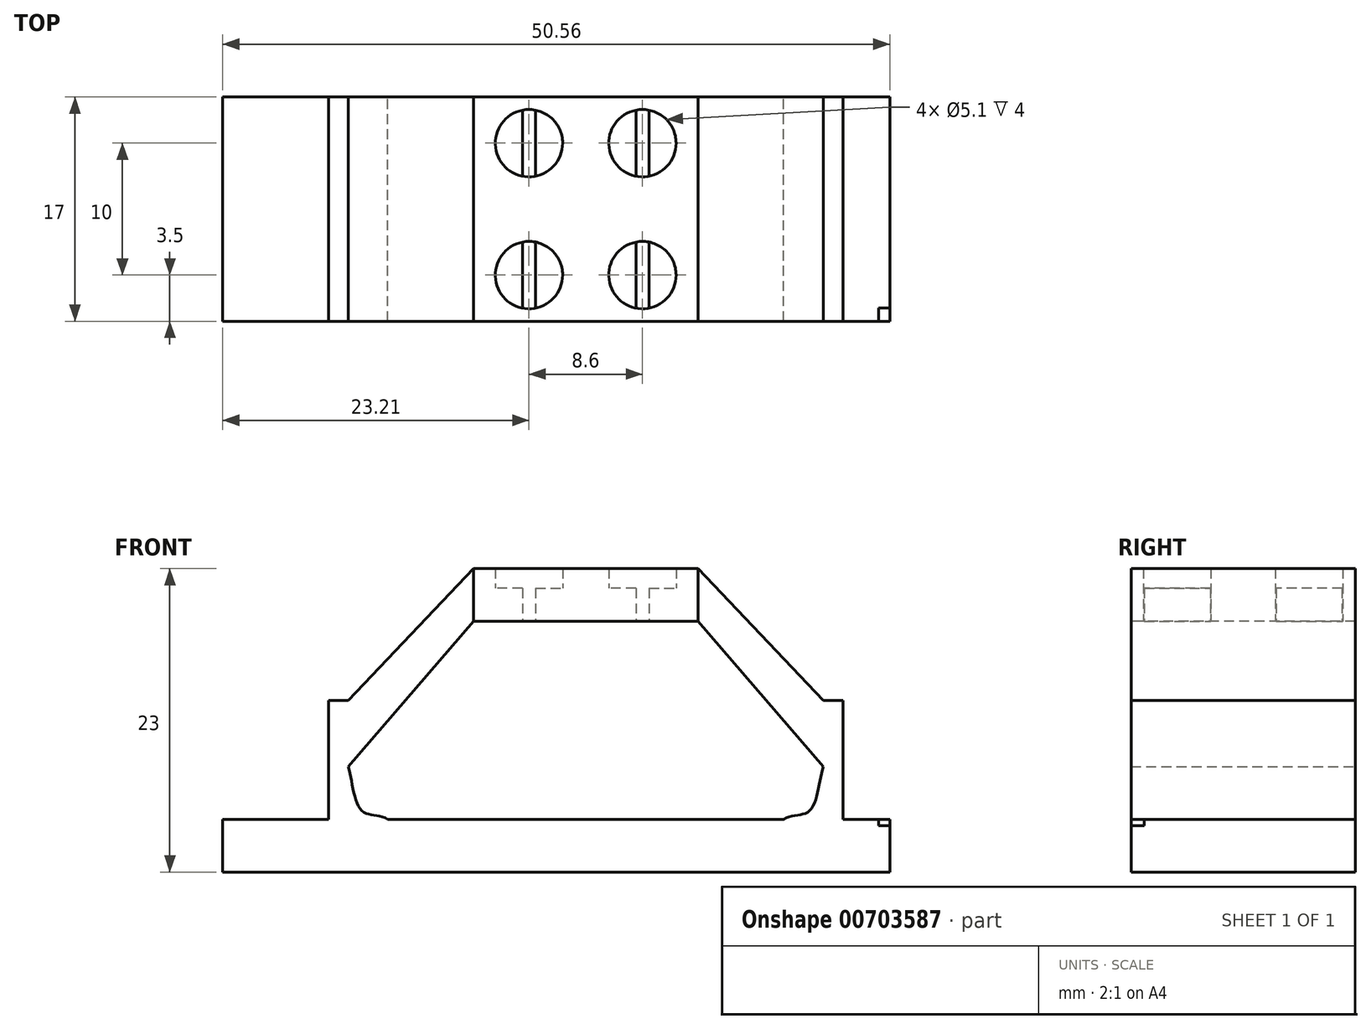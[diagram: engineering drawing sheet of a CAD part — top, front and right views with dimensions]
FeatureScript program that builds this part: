
annotation { "Feature Type Name" : "Feature", "Feature Type Description" : "" }
export const myFeature = defineFeature(function(context is Context, id is Id, definition is map)
    precondition{}
    {
        {
            assignVariable(context, id + "F0", {"name" : "Hollow", "anyValue" : 82});
        }
        {
            assignVariable(context, id + "F1", {"name" : "BaseThicknes", "anyValue" : 4});
        }
        {
            var Q0;
            Q0=qCreatedBy(makeId("Top.planeOp"),FACE);
            cPlane(context, id + "F2", {"entities" : qUnion([Q0]), "cplaneType" : CPlaneType.OFFSET, "offset" : (sqrt((sqrt((getVariable(context, 'Hollow') * getVariable(context, 'Hollow')) - ((getVariable(context, 'Hollow') / 2) * (getVariable(context, 'Hollow') / 2)))) * (sqrt((getVariable(context, 'Hollow') * getVariable(context, 'Hollow')) - ((getVariable(context, 'Hollow') / 2) * (getVariable(context, 'Hollow') / 2)))) - ((getVariable(context, 'Hollow') / 2) * (getVariable(context, 'Hollow') / 2)))) * mm, "width" : 150 * mm, "height" : 150 * mm});
        }
        {
            var Q0;
            Q0=qCreatedBy(id+"F2.planeOp",FACE);
            var sketch = newSketch(context, id + "F3", { "sketchPlane" : qUnion([Q0])});
            skPoint(sketch, "E0", {"position": v(0, 0) * mm});
            skSolve(sketch);
        }
        {
            var Q0;
            Q0=qCreatedBy(makeId("Top.planeOp"),FACE);
            var sketch = newSketch(context, id + "F4", { "sketchPlane" : qUnion([Q0])});
            skLineSegment(sketch, "E1.bottom", {"start": v(-41, 41) * mm, "end": v(41, 41) * mm});
            skLineSegment(sketch, "E1.top", {"start": v(-41, -41) * mm, "end": v(41, -41) * mm});
            skLineSegment(sketch, "E1.left", {"start": v(-41, 41) * mm, "end": v(-41, -41) * mm});
            skLineSegment(sketch, "E1.right", {"start": v(41, 41) * mm, "end": v(41, -41) * mm});
            skSolve(sketch);
        }
        {
            var Q0;
            Q0=qSketchRegion(id+"F4",true);
            extrude(context, id + "F5", {"entities" : qUnion([Q0]), "depth" : (getVariable(context, 'BaseThicknes')) * mm, "offsetDistance" : 25 * mm});
        }
        {
            var Q1;
            Q1=makeQuery(id+"F5.opExtrude","CAP_FACE",FACE,{"disambiguationData":[OSD([sQuery(id+"F4.wireOp",EDGE,"E1.bottom"),sQuery(id+"F4.wireOp",EDGE,"E1.top"),sQuery(id+"F4.wireOp",EDGE,"E1.left"),sQuery(id+"F4.wireOp",EDGE,"E1.right")])],"isStart":true});
            var Q2;
            Q2=sQuery(id+"F3.wireOp",VERTEX,"E0");
            loft(context, id + "F6", {"operationType" : NewBodyOperationType.INTERSECT, "sheetProfilesArray" : [{ "sheetProfileEntities" : qUnion([Q1]) }, { "sheetProfileEntities" : qUnion([Q2]) }]});
        }
        {
            var Q0;
            Q0=makeQuery(id+"F5.opExtrude","CAP_FACE",FACE,{"disambiguationData":[OSD([sQuery(id+"F4.wireOp",EDGE,"E1.bottom"),sQuery(id+"F4.wireOp",EDGE,"E1.top"),sQuery(id+"F4.wireOp",EDGE,"E1.left"),sQuery(id+"F4.wireOp",EDGE,"E1.right")])],"isStart":true});
            var sketch = newSketch(context, id + "F7", { "sketchPlane" : qUnion([Q0])});
            skCircle(sketch, "E2", {"center": v(-34.94, -34.94) * mm, "radius": 0.76 * mm});
            skCircle(sketch, "E3.MirrorC", {"center": v(34.94, -34.94) * mm, "radius": 0.76 * mm});
            skCircle(sketch, "E4.MirrorC", {"center": v(34.94, 34.94) * mm, "radius": 0.76 * mm});
            skCircle(sketch, "E5.MirrorC", {"center": v(-34.94, 34.94) * mm, "radius": 0.76 * mm});
            skCircle(sketch, "E6", {"center": v(-34.94, -34.94) * mm, "radius": 1.51 * mm});
            skCircle(sketch, "E7.MirrorC", {"center": v(-34.94, 34.94) * mm, "radius": 1.51 * mm});
            skCircle(sketch, "E8.MirrorC", {"center": v(34.94, -34.94) * mm, "radius": 1.51 * mm});
            skCircle(sketch, "E9.MirrorC", {"center": v(34.94, 34.94) * mm, "radius": 1.51 * mm});
            skSolve(sketch);
        }
        {
            var Q0;
            Q0=makeQuery(id+"F7.imprint","IMPRINT",FACE,{"disambiguationData":[TD([[makeQuery(id+"F7.imprint","IMPRINT",EDGE,{"derivedFrom":sQuery(id+"F7.wireOp",EDGE,"E2")}),1.0]])]});
            var Q1;
            Q1=makeQuery(id+"F7.imprint","IMPRINT",FACE,{"disambiguationData":[TD([[makeQuery(id+"F7.imprint","IMPRINT",EDGE,{"derivedFrom":sQuery(id+"F7.wireOp",EDGE,"E5.MirrorC")}),-1.0]])]});
            var Q2;
            Q2=makeQuery(id+"F7.imprint","IMPRINT",FACE,{"disambiguationData":[TD([[makeQuery(id+"F7.imprint","IMPRINT",EDGE,{"derivedFrom":sQuery(id+"F7.wireOp",EDGE,"E4.MirrorC")}),1.0]])]});
            var Q3;
            Q3=makeQuery(id+"F7.imprint","IMPRINT",FACE,{"disambiguationData":[TD([[makeQuery(id+"F7.imprint","IMPRINT",EDGE,{"derivedFrom":sQuery(id+"F7.wireOp",EDGE,"E3.MirrorC")}),-1.0]])]});
            extrude(context, id + "F8", {"entities" : qUnion([Q0, Q1, Q2, Q3]), "operationType" : NewBodyOperationType.REMOVE, "oppositeDirection" : true, "depth" : 25 * mm, "offsetDistance" : 25 * mm});
        }
        {
            var Q0;
            Q0=makeQuery(id+"F7.imprint","IMPRINT",FACE,{"disambiguationData":[TD([[makeQuery(id+"F7.imprint","IMPRINT",EDGE,{"derivedFrom":sQuery(id+"F7.wireOp",EDGE,"E5.MirrorC")}),1.0]])]});
            var Q1;
            Q1=makeQuery(id+"F7.imprint","IMPRINT",FACE,{"disambiguationData":[TD([[makeQuery(id+"F7.imprint","IMPRINT",EDGE,{"derivedFrom":sQuery(id+"F7.wireOp",EDGE,"E4.MirrorC")}),-1.0]])]});
            var Q2;
            Q2=makeQuery(id+"F7.imprint","IMPRINT",FACE,{"disambiguationData":[TD([[makeQuery(id+"F7.imprint","IMPRINT",EDGE,{"derivedFrom":sQuery(id+"F7.wireOp",EDGE,"E2")}),-1.0]])]});
            var Q3;
            Q3=makeQuery(id+"F7.imprint","IMPRINT",FACE,{"disambiguationData":[TD([[makeQuery(id+"F7.imprint","IMPRINT",EDGE,{"derivedFrom":sQuery(id+"F7.wireOp",EDGE,"E3.MirrorC")}),1.0]])]});
            extrude(context, id + "F9", {"entities" : qUnion([Q0, Q1, Q2, Q3]), "operationType" : NewBodyOperationType.REMOVE, "oppositeDirection" : true, "depth" : 2 * mm, "offsetDistance" : 25 * mm});
        }
        {
            var Q0;
            Q0=makeQuery(id+"F5.opExtrude","CAP_FACE",FACE,{"disambiguationData":[OSD([sQuery(id+"F4.wireOp",EDGE,"E1.bottom"),sQuery(id+"F4.wireOp",EDGE,"E1.top"),sQuery(id+"F4.wireOp",EDGE,"E1.left"),sQuery(id+"F4.wireOp",EDGE,"E1.right")])],"isStart":false});
            var sketch = newSketch(context, id + "F10", { "sketchPlane" : qUnion([Q0])});
            skLineSegment(sketch, "E10.bottom", {"start": v(-30, 29.5) * mm, "end": v(-26.3, 29.5) * mm});
            skLineSegment(sketch, "E10.top", {"start": v(-30, -16.5) * mm, "end": v(-26.3, -16.5) * mm});
            skLineSegment(sketch, "E10.left", {"start": v(-30, 29.5) * mm, "end": v(-30, -16.5) * mm});
            skLineSegment(sketch, "E10.right", {"start": v(-19.5, 29.5) * mm, "end": v(-19.5, -16.5) * mm});
            skLineSegment(sketch, "E11.bottom", {"start": v(-31.5, 31.5) * mm, "end": v(-26.3, 31.5) * mm});
            skLineSegment(sketch, "E11.top", {"start": v(-31.5, -18.5) * mm, "end": v(-18, -18.5) * mm});
            skLineSegment(sketch, "E11.left", {"start": v(-31.5, 31.5) * mm, "end": v(-31.5, -18.5) * mm});
            skLineSegment(sketch, "E11.right", {"start": v(-18, 31.5) * mm, "end": v(-18, -18.5) * mm});
            skLineSegment(sketch, "E12", {"start": v(-30, 27.7) * mm, "end": v(-28, 27.7) * mm});
            skLineSegment(sketch, "E13", {"start": v(-30, 28.7) * mm, "end": v(-28, 28.7) * mm});
            skLineSegment(sketch, "E14.left", {"start": v(-21.5, 28.7) * mm, "end": v(-21.5, 27.7) * mm});
            skLineSegment(sketch, "E14.right", {"start": v(-28, 28.7) * mm, "end": v(-28, 27.7) * mm});
            skLineSegment(sketch, "E15", {"start": v(-18, 6.5) * mm, "end": v(-31.5, 6.5) * mm, "construction": true});
            skLineSegment(sketch, "E16.trimOffspring", {"start": v(-21.5, 27.7) * mm, "end": v(-19.5, 27.7) * mm});
            skLineSegment(sketch, "E17.trimOffspring", {"start": v(-21.5, 28.7) * mm, "end": v(-19.5, 28.7) * mm});
            skLineSegment(sketch, "E18.MirrorCS", {"start": v(-30, -15.7) * mm, "end": v(-28, -15.7) * mm});
            skLineSegment(sketch, "E19.MirrorCS", {"start": v(-30, -14.7) * mm, "end": v(-28, -14.7) * mm});
            skLineSegment(sketch, "E20.MirrorCS", {"start": v(-21.5, -15.7) * mm, "end": v(-21.5, -14.7) * mm});
            skLineSegment(sketch, "E21.MirrorCS", {"start": v(-21.5, -15.7) * mm, "end": v(-19.5, -15.7) * mm});
            skLineSegment(sketch, "E22.MirrorCS", {"start": v(-21.5, -14.7) * mm, "end": v(-19.5, -14.7) * mm});
            skLineSegment(sketch, "E23.MirrorCS", {"start": v(-28, -15.7) * mm, "end": v(-28, -14.7) * mm});
            skLineSegment(sketch, "E24", {"start": v(-26.3, 31.5) * mm, "end": v(-26.3, 29.5) * mm});
            skLineSegment(sketch, "E25", {"start": v(-23.2, 31.5) * mm, "end": v(-23.2, 29.5) * mm});
            skLineSegment(sketch, "E26.trimOffspring", {"start": v(-23.2, 31.5) * mm, "end": v(-18, 31.5) * mm});
            skLineSegment(sketch, "E27.trimOffspring", {"start": v(-23.2, 29.5) * mm, "end": v(-19.5, 29.5) * mm});
            skLineSegment(sketch, "E28.MirrorCS", {"start": v(-26.3, -18.5) * mm, "end": v(-26.3, -16.5) * mm});
            skLineSegment(sketch, "E29.MirrorCS", {"start": v(-23.2, -18.5) * mm, "end": v(-23.2, -16.5) * mm});
            skLineSegment(sketch, "E30.trimOffspring", {"start": v(-23.2, -16.5) * mm, "end": v(-19.5, -16.5) * mm});
            skLineSegment(sketch, "E31.MirrorCS", {"start": v(21.5, 28.7) * mm, "end": v(21.5, 27.7) * mm});
            skLineSegment(sketch, "E32.MirrorCS", {"start": v(21.5, 28.7) * mm, "end": v(19.5, 28.7) * mm});
            skLineSegment(sketch, "E33.MirrorCS", {"start": v(23.2, 29.5) * mm, "end": v(19.5, 29.5) * mm});
            skLineSegment(sketch, "E34.MirrorCS", {"start": v(23.2, 31.5) * mm, "end": v(23.2, 29.5) * mm});
            skLineSegment(sketch, "E35.MirrorCS", {"start": v(28, -15.7) * mm, "end": v(28, -14.7) * mm});
            skLineSegment(sketch, "E36.MirrorCS", {"start": v(21.5, -15.7) * mm, "end": v(19.5, -15.7) * mm});
            skLineSegment(sketch, "E37.MirrorCS", {"start": v(23.2, -16.5) * mm, "end": v(19.5, -16.5) * mm});
            skLineSegment(sketch, "E38.MirrorCS", {"start": v(30, -15.7) * mm, "end": v(28, -15.7) * mm});
            skLineSegment(sketch, "E39.MirrorCS", {"start": v(21.5, -14.7) * mm, "end": v(19.5, -14.7) * mm});
            skLineSegment(sketch, "E40.MirrorCS", {"start": v(30, 29.5) * mm, "end": v(26.3, 29.5) * mm});
            skLineSegment(sketch, "E41.MirrorCS", {"start": v(30, 28.7) * mm, "end": v(28, 28.7) * mm});
            skLineSegment(sketch, "E42.MirrorCS", {"start": v(30, -16.5) * mm, "end": v(26.3, -16.5) * mm});
            skLineSegment(sketch, "E43.MirrorCS", {"start": v(26.3, 31.5) * mm, "end": v(26.3, 29.5) * mm});
            skLineSegment(sketch, "E44.MirrorCS", {"start": v(21.5, -15.7) * mm, "end": v(21.5, -14.7) * mm});
            skLineSegment(sketch, "E45.MirrorCS", {"start": v(28, 28.7) * mm, "end": v(28, 27.7) * mm});
            skLineSegment(sketch, "E46.MirrorCS", {"start": v(30, -14.7) * mm, "end": v(28, -14.7) * mm});
            skLineSegment(sketch, "E47.MirrorCS", {"start": v(31.5, 31.5) * mm, "end": v(26.3, 31.5) * mm});
            skLineSegment(sketch, "E48.MirrorCS", {"start": v(21.5, 27.7) * mm, "end": v(19.5, 27.7) * mm});
            skLineSegment(sketch, "E49.MirrorCS", {"start": v(23.2, -18.5) * mm, "end": v(23.2, -16.5) * mm});
            skLineSegment(sketch, "E50.MirrorCS", {"start": v(30, 27.7) * mm, "end": v(28, 27.7) * mm});
            skLineSegment(sketch, "E51.MirrorCS", {"start": v(26.3, -18.5) * mm, "end": v(26.3, -16.5) * mm});
            skLineSegment(sketch, "E52.MirrorCS", {"start": v(23.2, 31.5) * mm, "end": v(18, 31.5) * mm});
            skLineSegment(sketch, "E53.MirrorCS", {"start": v(31.5, 31.5) * mm, "end": v(31.5, -18.5) * mm});
            skLineSegment(sketch, "E54.MirrorCS", {"start": v(30, 29.5) * mm, "end": v(30, -16.5) * mm});
            skLineSegment(sketch, "E55.MirrorCS", {"start": v(31.5, -18.5) * mm, "end": v(18, -18.5) * mm});
            skLineSegment(sketch, "E56.MirrorCS", {"start": v(19.5, 29.5) * mm, "end": v(19.5, -16.5) * mm});
            skLineSegment(sketch, "E57.MirrorCS", {"start": v(18, 31.5) * mm, "end": v(18, -18.5) * mm});
            skLineSegment(sketch, "E58.MirrorCS", {"start": v(18, 6.5) * mm, "end": v(31.5, 6.5) * mm, "construction": true});
            skSolve(sketch);
        }
        {
            var Q0;
            {var subQ5=sQuery(id+"F10.wireOp",EDGE,"E33.MirrorCS");Q0=makeQuery(id+"F10.imprint","IMPRINT",FACE,{"disambiguationData":[TD([[makeQuery(id+"F10.imprint","IMPRINT",EDGE,{"derivedFrom":subQ5}),-1.0]])]});}
            var Q1;
            {var subQ6=sQuery(id+"F10.wireOp",EDGE,"E40.MirrorCS");Q1=makeQuery(id+"F10.imprint","IMPRINT",FACE,{"disambiguationData":[TD([[makeQuery(id+"F10.imprint","IMPRINT",EDGE,{"derivedFrom":subQ6}),-1.0]])]});}
            var Q2;
            Q2=makeQuery(id+"F10.imprint","IMPRINT",FACE,{"disambiguationData":[TD([[makeQuery(id+"F10.imprint","IMPRINT",EDGE,{"derivedFrom":sQuery(id+"F10.wireOp",EDGE,"E31.MirrorCS")}),-1.0]])]});
            var Q3;
            {var subQ0=sQuery(id+"F10.wireOp",EDGE,"E41.MirrorCS");Q3=makeQuery(id+"F10.imprint","IMPRINT",FACE,{"disambiguationData":[TD([[makeQuery(id+"F10.imprint","IMPRINT",EDGE,{"derivedFrom":subQ0}),1.0]])]});}
            var Q4;
            {var subQ0=sQuery(id+"F10.wireOp",EDGE,"E36.MirrorCS");Q4=makeQuery(id+"F10.imprint","IMPRINT",FACE,{"disambiguationData":[TD([[makeQuery(id+"F10.imprint","IMPRINT",EDGE,{"derivedFrom":subQ0}),-1.0]])]});}
            var Q5;
            Q5=makeQuery(id+"F10.imprint","IMPRINT",FACE,{"disambiguationData":[TD([[makeQuery(id+"F10.imprint","IMPRINT",EDGE,{"derivedFrom":sQuery(id+"F10.wireOp",EDGE,"E35.MirrorCS")}),-1.0]])]});
            var Q6;
            Q6=makeQuery(id+"F10.imprint","IMPRINT",FACE,{"disambiguationData":[TD([[makeQuery(id+"F10.imprint","IMPRINT",EDGE,{"derivedFrom":sQuery(id+"F10.wireOp",EDGE,"E20.MirrorCS")}),-1.0]])]});
            var Q7;
            {var subQ0=sQuery(id+"F10.wireOp",EDGE,"E18.MirrorCS");Q7=makeQuery(id+"F10.imprint","IMPRINT",FACE,{"disambiguationData":[TD([[makeQuery(id+"F10.imprint","IMPRINT",EDGE,{"derivedFrom":subQ0}),1.0]])]});}
            var Q8;
            {var subQ6=sQuery(id+"F10.wireOp",EDGE,"E10.bottom");Q8=makeQuery(id+"F10.imprint","IMPRINT",FACE,{"disambiguationData":[TD([[makeQuery(id+"F10.imprint","IMPRINT",EDGE,{"derivedFrom":subQ6}),1.0]])]});}
            var Q9;
            {var subQ0=sQuery(id+"F10.wireOp",EDGE,"E11.right");Q9=makeQuery(id+"F10.imprint","IMPRINT",FACE,{"disambiguationData":[TD([[makeQuery(id+"F10.imprint","IMPRINT",EDGE,{"derivedFrom":subQ0}),-1.0]])]});}
            var Q10;
            {var subQ0=sQuery(id+"F10.wireOp",EDGE,"E12");Q10=makeQuery(id+"F10.imprint","IMPRINT",FACE,{"disambiguationData":[TD([[makeQuery(id+"F10.imprint","IMPRINT",EDGE,{"derivedFrom":subQ0}),1.0]])]});}
            var Q11;
            Q11=makeQuery(id+"F10.imprint","IMPRINT",FACE,{"disambiguationData":[TD([[makeQuery(id+"F10.imprint","IMPRINT",EDGE,{"derivedFrom":sQuery(id+"F10.wireOp",EDGE,"E14.left")}),1.0]])]});
            extrude(context, id + "F11", {"entities" : qUnion([Q0, Q1, Q2, Q3, Q4, Q5, Q6, Q7, Q8, Q9, Q10, Q11]), "operationType" : NewBodyOperationType.ADD, "depth" : 9 * mm, "offsetDistance" : 25 * mm});
        }
        {
            var Q0;
            Q0=qCreatedBy(makeId("Front.planeOp"),FACE);
            var sketch = newSketch(context, id + "F12", { "sketchPlane" : qUnion([Q0])});
            skLineSegment(sketch, "E59", {"start": v(-31.5, 4) * mm, "end": v(-34.5, 4) * mm});
            skLineSegment(sketch, "E60", {"start": v(-31.5, 4) * mm, "end": v(-31.5, 8) * mm});
            skPoint(sketch, "E61", {"position": v(-34.5, 4) * mm});
            skFitSpline(sketch, "E62", {"points": [v(-31.5, 8) * mm, v(-32.53, 4.65) * mm, v(-34.5, 4) * mm], "startDerivative": vector(-1.67, -5.36) * mm, "endDerivative": vector(-4.69, -2.88) * mm});
            skLineSegment(sketch, "E63", {"start": v(-24.75, 13.95) * mm, "end": v(-24.75, 2.35) * mm, "construction": true});
            skFitSpline(sketch, "E64.MirrorCS", {"points": [v(-18, 8) * mm, v(-16.97, 4.65) * mm, v(-15, 4) * mm], "startDerivative": vector(1.67, -5.36) * mm, "endDerivative": vector(4.69, -2.88) * mm});
            skFitSpline(sketch, "E65.MirrorCS", {"points": [v(18, 8) * mm, v(16.97, 4.65) * mm, v(15, 4) * mm], "startDerivative": vector(-1.67, -5.36) * mm, "endDerivative": vector(-4.69, -2.88) * mm});
            skFitSpline(sketch, "E66.MirrorCS", {"points": [v(31.5, 8) * mm, v(32.53, 4.65) * mm, v(34.5, 4) * mm], "startDerivative": vector(1.67, -5.36) * mm, "endDerivative": vector(4.69, -2.88) * mm});
            skLineSegment(sketch, "E67.MirrorCS", {"start": v(-18, 4) * mm, "end": v(-15, 4) * mm});
            skLineSegment(sketch, "E68.MirrorCS", {"start": v(18, 4) * mm, "end": v(15, 4) * mm});
            skLineSegment(sketch, "E69.MirrorCS", {"start": v(31.5, 4) * mm, "end": v(34.5, 4) * mm});
            skLineSegment(sketch, "E70.MirrorCS", {"start": v(-18, 4) * mm, "end": v(-18, 8) * mm});
            skLineSegment(sketch, "E71.MirrorCS", {"start": v(18, 4) * mm, "end": v(18, 8) * mm});
            skLineSegment(sketch, "E72.MirrorCS", {"start": v(31.5, 4) * mm, "end": v(31.5, 8) * mm});
            skSolve(sketch);
        }
        {
            var Q0;
            Q0=qSketchRegion(id+"F12",true);
            extrude(context, id + "F13", {"entities" : qUnion([Q0]), "operationType" : NewBodyOperationType.ADD, "depth" : 18.5 * mm, "offsetDistance" : 25 * mm, "hasSecondDirection" : true, "secondDirectionOppositeDirection" : true, "secondDirectionDepth" : 31.5 * mm});
        }
        {
            var Q0;
            Q0=qCreatedBy(makeId("Right.planeOp"),FACE);
            var sketch = newSketch(context, id + "F14", { "sketchPlane" : qUnion([Q0])});
            skCircle(sketch, "E73", {"center": v(17.5, 13) * mm, "radius": 9 * mm});
            skCircle(sketch, "E74", {"center": v(-3.5, 13) * mm, "radius": 9 * mm});
            skSolve(sketch);
        }
        {
            var Q0;
            Q0=makeQuery(id+"F14.imprint","IMPRINT",FACE,{"disambiguationData":[TD([[makeQuery(id+"F14.imprint","IMPRINT",EDGE,{"derivedFrom":sQuery(id+"F14.wireOp",EDGE,"E73")}),1.0]])]});
            extrude(context, id + "F15", {"entities" : qUnion([Q0]), "operationType" : NewBodyOperationType.REMOVE, "oppositeDirection" : true, "depth" : 50 * mm, "offsetDistance" : 25 * mm, "hasSecondDirection" : true, "secondDirectionOppositeDirection" : false, "secondDirectionDepth" : 52.3 * mm});
        }
        {
            var Q0;
            Q0=makeQuery(id+"F5.opExtrude","CAP_FACE",FACE,{"disambiguationData":[OSD([sQuery(id+"F4.wireOp",EDGE,"E1.bottom"),sQuery(id+"F4.wireOp",EDGE,"E1.top"),sQuery(id+"F4.wireOp",EDGE,"E1.left"),sQuery(id+"F4.wireOp",EDGE,"E1.right")])],"isStart":false});
            var sketch = newSketch(context, id + "F16", { "sketchPlane" : qUnion([Q0])});
            skLineSegment(sketch, "E75.bottom", {"start": v(-7.5, -21.5) * mm, "end": v(7.5, -21.5) * mm});
            skLineSegment(sketch, "E75.top", {"start": v(-7.5, -31.5) * mm, "end": v(7.5, -31.5) * mm});
            skLineSegment(sketch, "E75.left", {"start": v(-7.5, -21.5) * mm, "end": v(-7.5, -31.5) * mm});
            skLineSegment(sketch, "E75.right", {"start": v(7.5, -21.5) * mm, "end": v(7.5, -31.5) * mm});
            skSolve(sketch);
        }
        {
            var Q0;
            Q0=qSketchRegion(id+"F16",true);
            extrude(context, id + "F17", {"entities" : qUnion([Q0]), "operationType" : NewBodyOperationType.REMOVE, "oppositeDirection" : true, "depth" : 25 * mm, "offsetDistance" : 25 * mm});
        }
        {
            var Q0;
            Q0=makeQuery(id+"F5.opExtrude","CAP_FACE",FACE,{"disambiguationData":[OSD([sQuery(id+"F4.wireOp",EDGE,"E1.bottom"),sQuery(id+"F4.wireOp",EDGE,"E1.top"),sQuery(id+"F4.wireOp",EDGE,"E1.left"),sQuery(id+"F4.wireOp",EDGE,"E1.right")])],"isStart":true});
            var sketch = newSketch(context, id + "F18", { "sketchPlane" : qUnion([Q0])});
            skLineSegment(sketch, "E76.bottom", {"start": v(-9.5, 33.5) * mm, "end": v(9.5, 33.5) * mm});
            skLineSegment(sketch, "E76.top", {"start": v(-9.5, 19.5) * mm, "end": v(9.5, 19.5) * mm});
            skLineSegment(sketch, "E76.left", {"start": v(-9.5, 33.5) * mm, "end": v(-9.5, 19.5) * mm});
            skLineSegment(sketch, "E76.right", {"start": v(9.5, 33.5) * mm, "end": v(9.5, 19.5) * mm});
            skSolve(sketch);
        }
        {
            var Q0;
            Q0=qSketchRegion(id+"F18",true);
            extrude(context, id + "F19", {"entities" : qUnion([Q0]), "operationType" : NewBodyOperationType.REMOVE, "oppositeDirection" : true, "depth" : 2 * mm, "offsetDistance" : 25 * mm});
        }
        {
            var Q0;
            Q0=makeQuery(id+"F5.opExtrude","CAP_FACE",FACE,{"disambiguationData":[OSD([sQuery(id+"F4.wireOp",EDGE,"E1.bottom"),sQuery(id+"F4.wireOp",EDGE,"E1.top"),sQuery(id+"F4.wireOp",EDGE,"E1.left"),sQuery(id+"F4.wireOp",EDGE,"E1.right")])],"isStart":false});
            var sketch = newSketch(context, id + "F20", { "sketchPlane" : qUnion([Q0])});
            skLineSegment(sketch, "E77.bottom", {"start": v(-25.25, 23.5) * mm, "end": v(-24.25, 23.5) * mm});
            skLineSegment(sketch, "E77.top", {"start": v(-25.25, 18.5) * mm, "end": v(-24.25, 18.5) * mm});
            skLineSegment(sketch, "E77.left", {"start": v(-25.25, 23.5) * mm, "end": v(-25.25, 18.5) * mm});
            skLineSegment(sketch, "E77.right", {"start": v(-24.25, 23.5) * mm, "end": v(-24.25, 18.5) * mm});
            skLineSegment(sketch, "E78.bottom", {"start": v(-27.25, 21.5) * mm, "end": v(-22.25, 21.5) * mm});
            skLineSegment(sketch, "E78.top", {"start": v(-27.25, 20.5) * mm, "end": v(-22.25, 20.5) * mm});
            skLineSegment(sketch, "E78.left", {"start": v(-27.25, 21.5) * mm, "end": v(-27.25, 20.5) * mm});
            skLineSegment(sketch, "E78.right", {"start": v(-22.25, 21.5) * mm, "end": v(-22.25, 20.5) * mm});
            skLineSegment(sketch, "E79", {"start": v(-24.75, 32.18) * mm, "end": v(-24.75, -20.77) * mm, "construction": true});
            skLineSegment(sketch, "E80.bottom", {"start": v(24.2, -5.5) * mm, "end": v(25.2, -5.5) * mm});
            skLineSegment(sketch, "E80.top", {"start": v(24.2, -10.5) * mm, "end": v(25.2, -10.5) * mm});
            skLineSegment(sketch, "E80.left", {"start": v(24.2, -5.5) * mm, "end": v(24.2, -10.5) * mm});
            skLineSegment(sketch, "E80.right", {"start": v(25.2, -5.5) * mm, "end": v(25.2, -10.5) * mm});
            skLineSegment(sketch, "E81.bottom", {"start": v(22.2, -7.5) * mm, "end": v(27.2, -7.5) * mm});
            skLineSegment(sketch, "E81.top", {"start": v(22.2, -8.5) * mm, "end": v(27.2, -8.5) * mm});
            skLineSegment(sketch, "E81.left", {"start": v(22.2, -7.5) * mm, "end": v(22.2, -8.5) * mm});
            skLineSegment(sketch, "E81.right", {"start": v(27.2, -7.5) * mm, "end": v(27.2, -8.5) * mm});
            skLineSegment(sketch, "E82", {"start": v(24.7, 5.1) * mm, "end": v(24.7, -19.14) * mm, "construction": true});
            skText(sketch, "E83", { "text": "PW SW", "fontName": "OpenSans-Regular.ttf"});
            const initialGuessF20  = {"E83": [-0.00532, -0.01924, 1, 0, 0.00251]};
            skSetInitialGuess(sketch, initialGuessF20);
            skSolve(sketch);
        }
        {
            var Q0;
            Q0=qSketchRegion(id+"F20",true);
            extrude(context, id + "F21", {"entities" : qUnion([Q0]), "operationType" : NewBodyOperationType.REMOVE, "oppositeDirection" : true, "depth" : .5 * mm, "offsetDistance" : 25 * mm});
        }
        {
            var Q0;
            Q0=makeQuery(id+"F20.imprint","IMPRINT",FACE,{"disambiguationData":[TD([[makeQuery(id+"F20.imprint","IMPRINT",EDGE,{"derivedFrom":sQuery(id+"F20.wireOp",EDGE,"E83.sketch_text.stroke-35")}),-1.0]])]});
            var Q1;
            Q1=makeQuery(id+"F20.imprint","IMPRINT",FACE,{"disambiguationData":[TD([[makeQuery(id+"F20.imprint","IMPRINT",EDGE,{"derivedFrom":sQuery(id+"F20.wireOp",EDGE,"E83.sketch_text.stroke-60")}),-1.0]])]});
            var Q2;
            Q2=makeQuery(id+"F20.imprint","IMPRINT",FACE,{"disambiguationData":[TD([[makeQuery(id+"F20.imprint","IMPRINT",EDGE,{"derivedFrom":sQuery(id+"F20.wireOp",EDGE,"E83.sketch_text.stroke-15")}),-1.0]])]});
            var Q3;
            Q3=makeQuery(id+"F20.imprint","IMPRINT",FACE,{"disambiguationData":[TD([[makeQuery(id+"F20.imprint","IMPRINT",EDGE,{"derivedFrom":sQuery(id+"F20.wireOp",EDGE,"E83.sketch_text.stroke-0")}),-1.0]])]});
            extrude(context, id + "F22", {"entities" : qUnion([Q0, Q1, Q2, Q3]), "operationType" : NewBodyOperationType.REMOVE, "oppositeDirection" : true, "depth" : .5 * mm, "offsetDistance" : 25 * mm});
        }
        {
            var Q0;
            {var subQ15=sQuery(id+"F4.wireOp",EDGE,"E1.right");var subQ16=sQuery(id+"F4.wireOp",EDGE,"E1.left");var subQ17=sQuery(id+"F4.wireOp",EDGE,"E1.top");var subQ18=sQuery(id+"F4.wireOp",EDGE,"E1.bottom");var subQ19=makeQuery(id+"F5.opExtrude","CAP_FACE",FACE,{"disambiguationData":[OSD([subQ18,subQ17,subQ16,subQ15])],"isStart":false});Q0=makeQuery(id+"F21.boolean.opBoolean","SPLIT",FACE,{"disambiguationData":[TD([makeQuery(id+"F8.boolean.opBoolean","COPY",FACE,{"derivedFrom":makeQuery(id+"F8.opExtrude","SWEPT_FACE",FACE,{"disambiguationData":[OSD([sQuery(id+"F7.wireOp",EDGE,"E2")])]})})])],"derivedFrom":subQ19});}
            cPlane(context, id + "F23", {"entities" : qUnion([Q0]), "cplaneType" : CPlaneType.OFFSET, "offset" : 15 * mm, "width" : 150 * mm, "height" : 150 * mm});
        }
        {
            var Q0;
            Q0=qCreatedBy(id+"F23.planeOp",FACE);
            var sketch = newSketch(context, id + "F24", { "sketchPlane" : qUnion([Q0])});
            skLineSegment(sketch, "E84.bottom", {"start": v(-8.5, 8.5) * mm, "end": v(-4.8, 8.5) * mm});
            skLineSegment(sketch, "E84.top", {"start": v(-8.5, -8.5) * mm, "end": v(8.5, -8.5) * mm});
            skLineSegment(sketch, "E84.left", {"start": v(-8.5, 8.5) * mm, "end": v(-8.5, -8.5) * mm});
            skLineSegment(sketch, "E84.right", {"start": v(8.5, 8.5) * mm, "end": v(8.5, -8.5) * mm});
            skLineSegment(sketch, "E85.left", {"start": v(-4.8, 7.5) * mm, "end": v(-4.8, 2.5) * mm});
            skLineSegment(sketch, "E85.right", {"start": v(-3.8, 7.5) * mm, "end": v(-3.8, 2.5) * mm});
            skLineSegment(sketch, "E86.trimOffspring", {"start": v(-3.8, 8.5) * mm, "end": v(8.5, 8.5) * mm});
            skLineSegment(sketch, "E87.MirrorCS", {"start": v(3.8, 7.5) * mm, "end": v(3.8, 2.5) * mm});
            skLineSegment(sketch, "E88.MirrorCS", {"start": v(4.8, -7.5) * mm, "end": v(4.8, -2.5) * mm});
            skLineSegment(sketch, "E89.MirrorCS", {"start": v(3.8, -7.5) * mm, "end": v(3.8, -2.5) * mm});
            skLineSegment(sketch, "E90.MirrorCS", {"start": v(-4.8, -7.5) * mm, "end": v(-4.8, -2.5) * mm});
            skLineSegment(sketch, "E91.MirrorCS", {"start": v(-3.8, -7.5) * mm, "end": v(-3.8, -2.5) * mm});
            skCircle(sketch, "E92", {"center": v(-4.3, 5) * mm, "radius": 2.55 * mm});
            skCircle(sketch, "E93", {"center": v(4.3, 5) * mm, "radius": 2.55 * mm});
            skCircle(sketch, "E94", {"center": v(-4.3, -5) * mm, "radius": 2.55 * mm});
            skCircle(sketch, "E95", {"center": v(4.3, -5) * mm, "radius": 2.55 * mm});
            skLineSegment(sketch, "E96", {"start": v(-4.8, 8.5) * mm, "end": v(-3.8, 8.5) * mm});
            skPoint(sketch, "E97.orphan", {"position": v(3.8, 8.5) * mm});
            skPoint(sketch, "E98.orphan", {"position": v(4.8, 8.5) * mm});
            skPoint(sketch, "E99.MirrorCS.end.orphan", {"position": v(4.8, 2.5) * mm});
            skPoint(sketch, "E100.orphan", {"position": v(-4.8, -8.5) * mm});
            skPoint(sketch, "E101.orphan", {"position": v(-3.8, -8.5) * mm});
            skPoint(sketch, "E102.orphan", {"position": v(3.8, -8.5) * mm});
            skPoint(sketch, "E103.orphan", {"position": v(4.8, -8.5) * mm});
            skLineSegment(sketch, "E104", {"start": v(4.8, 2.5) * mm, "end": v(4.8, 7.5) * mm});
            skSolve(sketch);
        }
        {
            var Q0;
            Q0=makeQuery(id+"F24.imprint","IMPRINT",FACE,{"disambiguationData":[TD([[makeQuery(id+"F24.imprint","IMPRINT",EDGE,{"derivedFrom":sQuery(id+"F24.wireOp",EDGE,"E84.bottom")}),-1.0]])]});
            extrude(context, id + "F25", {"entities" : qUnion([Q0]), "depth" : 4 * mm, "offsetDistance" : 25 * mm});
        }
        {
            var Q0;
            {var subQ1=sQuery(id+"F10.wireOp",EDGE,"E11.right");var subQ2=sQuery(id+"F10.wireOp",EDGE,"E11.top");Q0=makeQuery(id+"F15.boolean.opBoolean","SPLIT",FACE,{"disambiguationData":[TD([makeQuery(id+"F11.opExtrude","SWEPT_FACE",FACE,{"disambiguationData":[OSD([subQ2]),TDD([makeQuery(id+"F10.imprint","IMPRINT",EDGE,{"disambiguationData":[TD([[makeQuery(id+"F10.imprint","INTERSECT",VERTEX,{"derivedFrom":[subQ2,subQ1]}),1.0]])],"derivedFrom":subQ2})])]})])],"derivedFrom":makeQuery(id+"F11.opExtrude","SWEPT_FACE",FACE,{"disambiguationData":[OSD([subQ1])]})});}
            var Q1;
            Q1=makeQuery(id+"F25.opExtrude","SWEPT_FACE",FACE,{"disambiguationData":[OSD([sQuery(id+"F24.wireOp",EDGE,"E84.left")])]});
            loft(context, id + "F26", {"sheetProfilesArray" : [{ "sheetProfileEntities" : qUnion([Q0]) }, { "sheetProfileEntities" : qUnion([Q1]) }]});
        }
        {
            var Q0;
            {var subQ1=sQuery(id+"F10.wireOp",EDGE,"E55.MirrorCS");var subQ2=sQuery(id+"F10.wireOp",EDGE,"E49.MirrorCS");var subQ3=sQuery(id+"F10.wireOp",EDGE,"E57.MirrorCS");Q0=makeQuery(id+"F15.boolean.opBoolean","SPLIT",FACE,{"disambiguationData":[TD([makeQuery(id+"F11.opExtrude","SWEPT_FACE",FACE,{"disambiguationData":[OSD([subQ1]),TDD([makeQuery(id+"F10.imprint","IMPRINT",EDGE,{"disambiguationData":[TD([[makeQuery(id+"F10.imprint","INTERSECT",VERTEX,{"derivedFrom":[subQ2,subQ1]}),-1.0]])],"derivedFrom":subQ1})])]})])],"derivedFrom":makeQuery(id+"F11.opExtrude","SWEPT_FACE",FACE,{"disambiguationData":[OSD([subQ3])]})});}
            var Q1;
            Q1=makeQuery(id+"F25.opExtrude","SWEPT_FACE",FACE,{"disambiguationData":[OSD([sQuery(id+"F24.wireOp",EDGE,"E84.right")])]});
            loft(context, id + "F27", {"sheetProfilesArray" : [{ "sheetProfileEntities" : qUnion([Q0]) }, { "sheetProfileEntities" : qUnion([Q1]) }]});
        }
        {
            var Q0;
            {var subQ0=sQuery(id+"F10.wireOp",EDGE,"E30.trimOffspring");var subQ1=sQuery(id+"F10.wireOp",EDGE,"E29.MirrorCS");var subQ2=sQuery(id+"F10.wireOp",EDGE,"E10.right");var subQ3=sQuery(id+"F10.wireOp",EDGE,"E21.MirrorCS");var subQ4=sQuery(id+"F10.wireOp",EDGE,"E16.trimOffspring");var subQ5=sQuery(id+"F10.wireOp",EDGE,"E22.MirrorCS");var subQ6=sQuery(id+"F10.wireOp",EDGE,"E11.right");var subQ7=sQuery(id+"F10.wireOp",EDGE,"E20.MirrorCS");var subQ8=sQuery(id+"F10.wireOp",EDGE,"E11.top");Q0=makeQuery(id+"F15.boolean.opBoolean","SPLIT",FACE,{"disambiguationData":[TD([makeQuery(id+"F11.opExtrude","SWEPT_FACE",FACE,{"disambiguationData":[OSD([subQ7])]})])],"derivedFrom":makeQuery(id+"F11.opExtrude","CAP_FACE",FACE,{"disambiguationData":[OSD([subQ2,subQ8,subQ6,sQuery(id+"F10.wireOp",EDGE,"E14.left"),subQ4,sQuery(id+"F10.wireOp",EDGE,"E17.trimOffspring"),subQ7,subQ3,subQ5,sQuery(id+"F10.wireOp",EDGE,"E25"),sQuery(id+"F10.wireOp",EDGE,"E26.trimOffspring"),sQuery(id+"F10.wireOp",EDGE,"E27.trimOffspring"),subQ1,subQ0])],"isStart":false})});}
            var sketch = newSketch(context, id + "F28", { "sketchPlane" : qUnion([Q0])});
            skLineSegment(sketch, "E105", {"start": v(-19.5, 5) * mm, "end": v(-19.5, -5) * mm});
            skLineSegment(sketch, "E106", {"start": v(-19.5, -5) * mm, "end": v(-18, -3.5) * mm});
            skLineSegment(sketch, "E107", {"start": v(-18, -3.5) * mm, "end": v(-18, 3.5) * mm});
            skLineSegment(sketch, "E108", {"start": v(-18, 3.5) * mm, "end": v(-19.5, 5) * mm});
            skLineSegment(sketch, "E109.MirrorCS", {"start": v(18, 3.5) * mm, "end": v(19.5, 5) * mm});
            skLineSegment(sketch, "E110.MirrorCS", {"start": v(19.5, -5) * mm, "end": v(18, -3.5) * mm});
            skLineSegment(sketch, "E111.MirrorCS", {"start": v(19.5, 5) * mm, "end": v(19.5, -5) * mm});
            skLineSegment(sketch, "E112.MirrorCS", {"start": v(18, -3.5) * mm, "end": v(18, 3.5) * mm});
            skSolve(sketch);
        }
        {
            var Q0;
            Q0=qSketchRegion(id+"F28",true);
            extrude(context, id + "F29", {"entities" : qUnion([Q0]), "operationType" : NewBodyOperationType.REMOVE, "oppositeDirection" : true, "depth" : 4 * mm, "offsetDistance" : 25 * mm});
        }
        {
            var Q0;
            Q0=qSketchRegion(id+"F28",true);
            extrude(context, id + "F30", {"entities" : qUnion([Q0]), "operationType" : NewBodyOperationType.ADD, "depth" : -4 * mm, "offsetDistance" : 25 * mm});
        }
        {
            var Q0;
            Q0=makeQuery(id+"F25.opExtrude","CAP_FACE",FACE,{"disambiguationData":[OSD([sQuery(id+"F24.wireOp",EDGE,"E84.bottom"),sQuery(id+"F24.wireOp",EDGE,"E84.top"),sQuery(id+"F24.wireOp",EDGE,"E84.left"),sQuery(id+"F24.wireOp",EDGE,"E84.right"),sQuery(id+"F24.wireOp",EDGE,"2IplUNgi-tkBv-9E8a-ZFnB-auiuJyXHGnih"),sQuery(id+"F24.wireOp",EDGE,"E85.left"),sQuery(id+"F24.wireOp",EDGE,"E85.right"),sQuery(id+"F24.wireOp",EDGE,"E86.trimOffspring"),sQuery(id+"F24.wireOp",EDGE,"dbc6eed9-552c-4b0d-aad6-60334d5a8f2e0.MirrorCS"),sQuery(id+"F24.wireOp",EDGE,"E99.MirrorCS"),sQuery(id+"F24.wireOp",EDGE,"E87.MirrorCS"),sQuery(id+"F24.wireOp",EDGE,"1bd0f054-9f5b-46f9-b1dd-c3be90d0bcb60.MirrorCS"),sQuery(id+"F24.wireOp",EDGE,"E88.MirrorCS"),sQuery(id+"F24.wireOp",EDGE,"E89.MirrorCS"),sQuery(id+"F24.wireOp",EDGE,"f50dec66-58dc-4cda-8118-78d90768280c0.MirrorCS"),sQuery(id+"F24.wireOp",EDGE,"E90.MirrorCS"),sQuery(id+"F24.wireOp",EDGE,"E91.MirrorCS")])],"isStart":false});
            var sketch = newSketch(context, id + "F31", { "sketchPlane" : qUnion([Q0])});
            skLineSegment(sketch, "E113.bottom", {"start": v(23.05, 8.5) * mm, "end": v(-27.5, 8.5) * mm});
            skLineSegment(sketch, "E113.top", {"start": v(23.05, -8.5) * mm, "end": v(-27.5, -8.5) * mm});
            skLineSegment(sketch, "E113.left", {"start": v(23.05, 8.5) * mm, "end": v(23.05, -8.5) * mm});
            skLineSegment(sketch, "E113.right", {"start": v(-27.5, 8.5) * mm, "end": v(-27.5, -8.5) * mm});
            skSolve(sketch);
        }
        {
            var Q0;
            Q0=qSketchRegion(id+"F31",true);
            extrude(context, id + "F32", {"entities" : qUnion([Q0]), "operationType" : NewBodyOperationType.INTERSECT, "depth" : -50 * mm, "offsetDistance" : 25 * mm});
        }
        {
            var Q0;
            {var subQ0=sQuery(id+"F24.wireOp",EDGE,"E85.left");Q0=makeQuery(id+"F24.imprint","IMPRINT",FACE,{"disambiguationData":[TD([[makeQuery(id+"F24.imprint","IMPRINT",EDGE,{"derivedFrom":subQ0}),-1.0]])]});}
            var Q1;
            {var subQ0=sQuery(id+"F24.wireOp",EDGE,"E85.right");Q1=makeQuery(id+"F24.imprint","IMPRINT",FACE,{"disambiguationData":[TD([[makeQuery(id+"F24.imprint","IMPRINT",EDGE,{"derivedFrom":subQ0}),1.0]])]});}
            var Q2;
            {var subQ0=sQuery(id+"F24.wireOp",EDGE,"E87.MirrorCS");Q2=makeQuery(id+"F24.imprint","IMPRINT",FACE,{"disambiguationData":[TD([[makeQuery(id+"F24.imprint","IMPRINT",EDGE,{"derivedFrom":subQ0}),-1.0]])]});}
            var Q3;
            {var subQ0=sQuery(id+"F24.wireOp",EDGE,"E104");Q3=makeQuery(id+"F24.imprint","IMPRINT",FACE,{"disambiguationData":[TD([[makeQuery(id+"F24.imprint","IMPRINT",EDGE,{"derivedFrom":subQ0}),-1.0]])]});}
            var Q4;
            {var subQ0=sQuery(id+"F24.wireOp",EDGE,"E90.MirrorCS");Q4=makeQuery(id+"F24.imprint","IMPRINT",FACE,{"disambiguationData":[TD([[makeQuery(id+"F24.imprint","IMPRINT",EDGE,{"derivedFrom":subQ0}),1.0]])]});}
            var Q5;
            {var subQ0=sQuery(id+"F24.wireOp",EDGE,"E91.MirrorCS");Q5=makeQuery(id+"F24.imprint","IMPRINT",FACE,{"disambiguationData":[TD([[makeQuery(id+"F24.imprint","IMPRINT",EDGE,{"derivedFrom":subQ0}),-1.0]])]});}
            var Q6;
            {var subQ0=sQuery(id+"F24.wireOp",EDGE,"E89.MirrorCS");Q6=makeQuery(id+"F24.imprint","IMPRINT",FACE,{"disambiguationData":[TD([[makeQuery(id+"F24.imprint","IMPRINT",EDGE,{"derivedFrom":subQ0}),1.0]])]});}
            var Q7;
            {var subQ0=sQuery(id+"F24.wireOp",EDGE,"E88.MirrorCS");Q7=makeQuery(id+"F24.imprint","IMPRINT",FACE,{"disambiguationData":[TD([[makeQuery(id+"F24.imprint","IMPRINT",EDGE,{"derivedFrom":subQ0}),-1.0]])]});}
            extrude(context, id + "F33", {"entities" : qUnion([Q0, Q1, Q2, Q3, Q4, Q5, Q6, Q7]), "operationType" : NewBodyOperationType.ADD, "depth" : 2.5 * mm, "offsetDistance" : 25 * mm});
        }
    });
